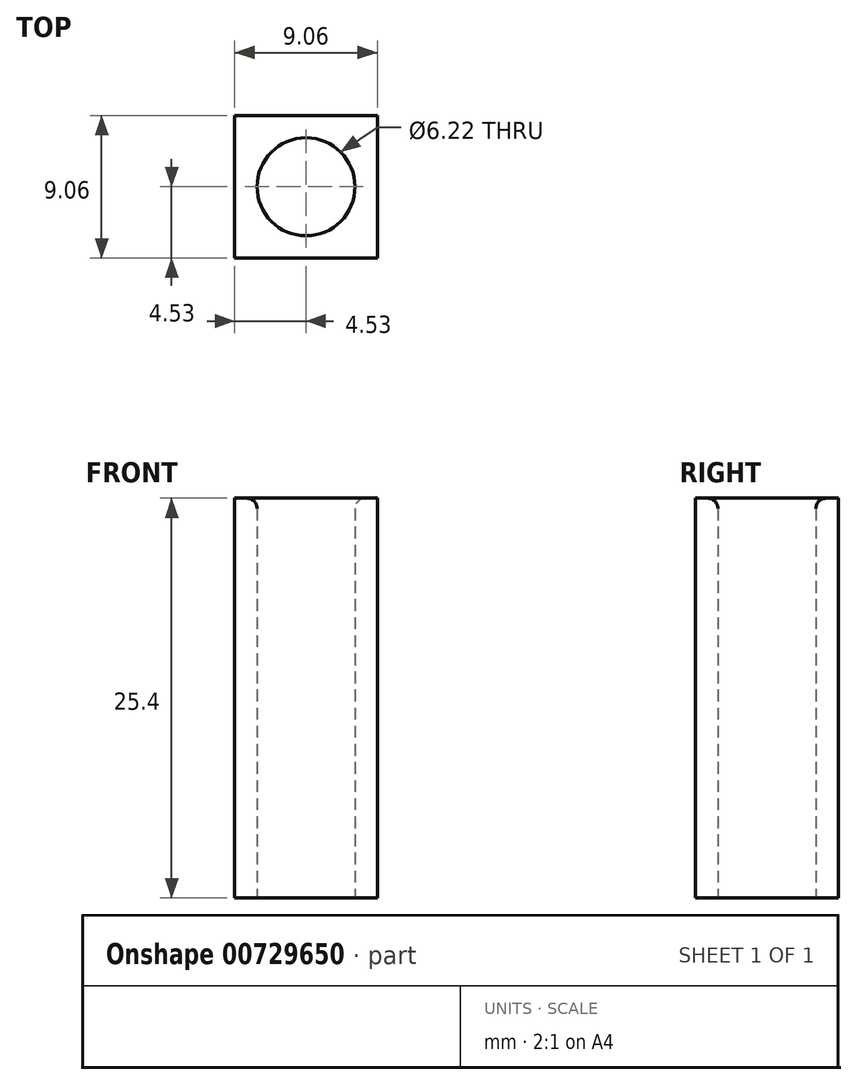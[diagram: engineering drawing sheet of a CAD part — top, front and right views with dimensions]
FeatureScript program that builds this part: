
annotation { "Feature Type Name" : "Feature", "Feature Type Description" : "" }
export const myFeature = defineFeature(function(context is Context, id is Id, definition is map)
    precondition{}
    {
        {
            var Q0;
            Q0=qCreatedBy(makeId("Top.planeOp"),FACE);
            var sketch = newSketch(context, id + "F0", { "sketchPlane" : qUnion([Q0])});
            skLineSegment(sketch, "E0.bottom", {"start": v(4.53, 4.53) * mm, "end": v(-4.53, 4.53) * mm});
            skLineSegment(sketch, "E0.top", {"start": v(4.53, -4.53) * mm, "end": v(-4.53, -4.53) * mm});
            skLineSegment(sketch, "E0.left", {"start": v(4.53, 4.53) * mm, "end": v(4.53, -4.53) * mm});
            skLineSegment(sketch, "E0.right", {"start": v(-4.53, 4.53) * mm, "end": v(-4.53, -4.53) * mm});
            skPoint(sketch, "E0.middle", {"position": v(0, 0) * mm});
            skCircle(sketch, "E1", {"center": v(0, 0) * mm, "radius": 3.11 * mm});
            skSolve(sketch);
        }
        {
            var Q0;
            Q0 = qSketchRegion(id + "F0", true);
            extrude(context, id + "F1", {"entities" : qUnion([Q0]), "depth" : 25.4 * mm, "offsetDistance" : 25.4 * mm});
        }
        {
            var Q0;
            Q0=makeQuery(id+"F1.opExtrude","CAP_EDGE",EDGE,{"disambiguationData":[OSD([sQuery(id+"F0.wireOp",EDGE,"E1")])],"isStart":false});
            fillet(context, id + "F2", {"entities" : qUnion([Q0]), "radius" : 0.66 * mm, "tangentPropagation" : true, "allowEdgeOverflow" : false});
        }
    });
